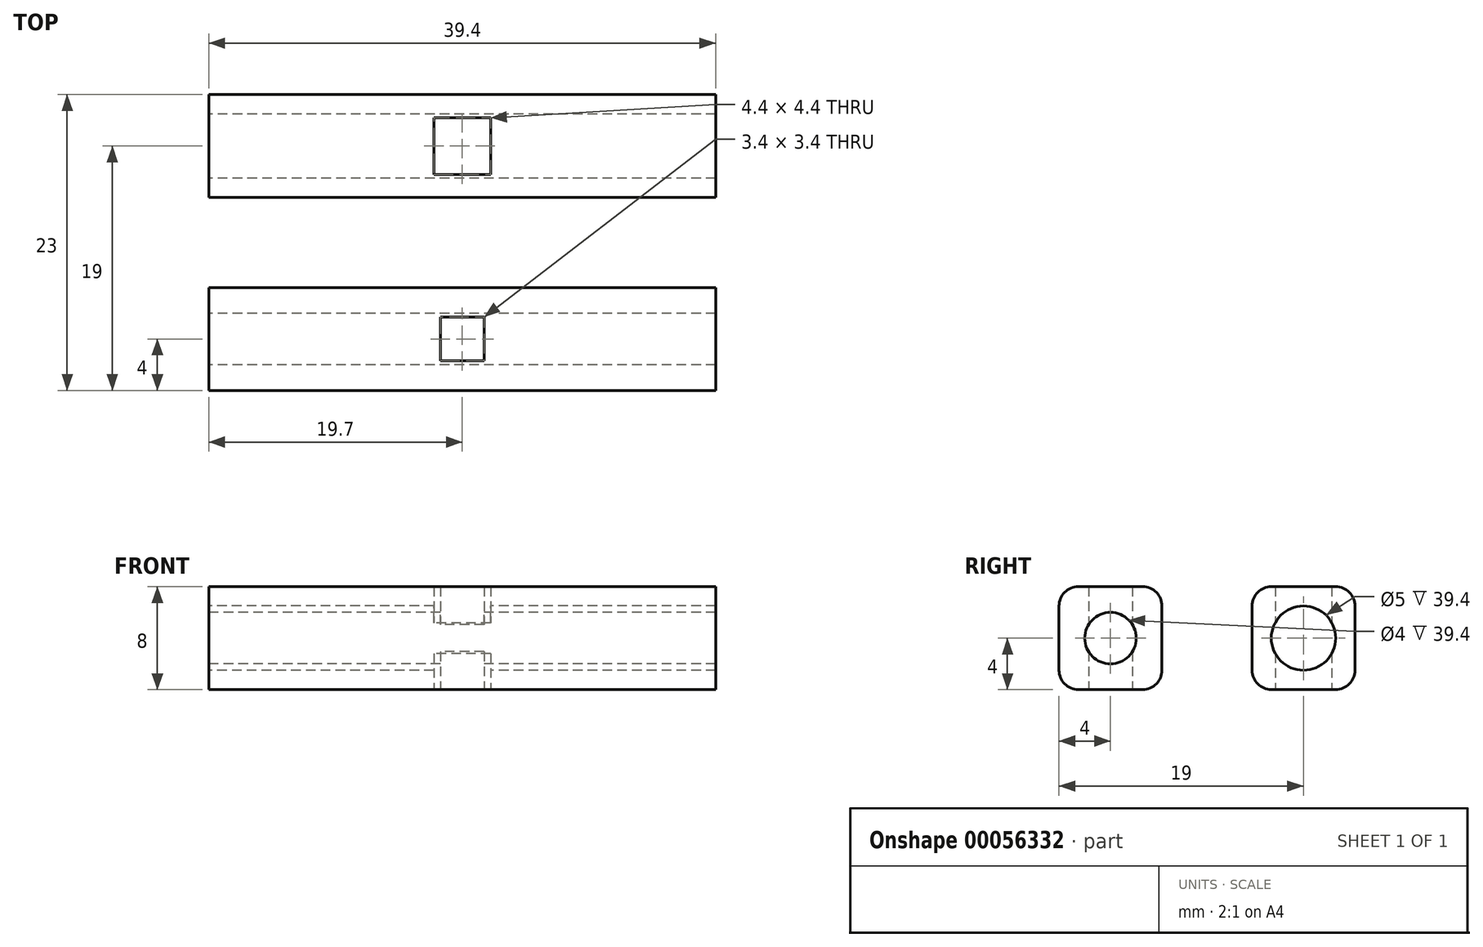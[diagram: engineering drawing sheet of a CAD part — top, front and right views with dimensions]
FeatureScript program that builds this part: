
annotation { "Feature Type Name" : "Feature", "Feature Type Description" : "" }
export const myFeature = defineFeature(function(context is Context, id is Id, definition is map)
    precondition{}
    {
        {
            var Q0;
            Q0=qCreatedBy(makeId("Top.planeOp"),FACE);
            var sketch = newSketch(context, id + "F0", { "sketchPlane" : qUnion([Q0])});
            skLineSegment(sketch, "E0.rect.bottom", {"start": v(19.7, 2) * mm, "end": v(-19.7, 2) * mm, "construction": true});
            skLineSegment(sketch, "E0.rect.top", {"start": v(19.7, -2) * mm, "end": v(-19.7, -2) * mm, "construction": true});
            skLineSegment(sketch, "E0.rect.left", {"start": v(19.7, 2) * mm, "end": v(19.7, -2) * mm});
            skLineSegment(sketch, "E0.rect.right", {"start": v(-19.7, 2) * mm, "end": v(-19.7, -2) * mm});
            skPoint(sketch, "E0.rect.middle", {"position": v(0, 0) * mm});
            skLineSegment(sketch, "E1.rect.bottom", {"start": v(19.7, 4) * mm, "end": v(-19.7, 4) * mm});
            skLineSegment(sketch, "E1.rect.top", {"start": v(19.7, -4) * mm, "end": v(-19.7, -4) * mm});
            skLineSegment(sketch, "E1.rect.left", {"start": v(19.7, 4) * mm, "end": v(19.7, -4) * mm});
            skLineSegment(sketch, "E1.rect.right", {"start": v(-19.7, 4) * mm, "end": v(-19.7, -4) * mm});
            skLineSegment(sketch, "E2.rect.bottom", {"start": v(1.7, 1.7) * mm, "end": v(-1.7, 1.7) * mm});
            skLineSegment(sketch, "E2.rect.top", {"start": v(1.7, -1.7) * mm, "end": v(-1.7, -1.7) * mm});
            skLineSegment(sketch, "E2.rect.left", {"start": v(1.7, 1.7) * mm, "end": v(1.7, -1.7) * mm});
            skLineSegment(sketch, "E2.rect.right", {"start": v(-1.7, 1.7) * mm, "end": v(-1.7, -1.7) * mm});
            skSolve(sketch);
        }
        {
            var Q0;
            Q0=qSketchRegion(id+"F0",true);
            extrude(context, id + "F1", {"entities" : qUnion([Q0]), "depth" : 8 * mm});
        }
        {
            var Q0;
            Q0=makeQuery(id+"F1.opExtrude","SWEPT_FACE",FACE,{"disambiguationData":[OSD([sQuery(id+"F0.wireOp",EDGE,"E1.rect.right")])]});
            var sketch = newSketch(context, id + "F2", { "sketchPlane" : qUnion([Q0])});
            skCircle(sketch, "E3", {"center": v(0, 4) * mm, "radius": 2 * mm});
            skPoint(sketch, "E3.centerSnap0", {"position": v(4, 4) * mm});
            skPoint(sketch, "E3.centerSnap1", {"position": v(0, 8) * mm});
            skSolve(sketch);
        }
        {
            var Q0;
            Q0=qSketchRegion(id+"F2",true);
            extrude(context, id + "F3", {"entities" : qUnion([Q0]), "operationType" : NewBodyOperationType.REMOVE, "endBound" : BoundingType.THROUGH_ALL, "oppositeDirection" : true, "depth" : 25 * mm});
        }
        {
            var Q0;
            Q0=makeQuery(id+"F1.opExtrude","CAP_EDGE",EDGE,{"disambiguationData":[OSD([sQuery(id+"F0.wireOp",EDGE,"E1.rect.top")])],"isStart":false});
            var Q1;
            Q1=makeQuery(id+"F1.opExtrude","CAP_EDGE",EDGE,{"disambiguationData":[OSD([sQuery(id+"F0.wireOp",EDGE,"E1.rect.bottom")])],"isStart":false});
            var Q2;
            Q2=makeQuery(id+"F1.opExtrude","CAP_EDGE",EDGE,{"disambiguationData":[OSD([sQuery(id+"F0.wireOp",EDGE,"E1.rect.top")])],"isStart":true});
            var Q3;
            Q3=makeQuery(id+"F1.opExtrude","CAP_EDGE",EDGE,{"disambiguationData":[OSD([sQuery(id+"F0.wireOp",EDGE,"E1.rect.bottom")])],"isStart":true});
            fillet(context, id + "F4", {"entities" : qUnion([Q0, Q1, Q2, Q3]), "radius" : 1.5 * mm, "tangentPropagation" : true, "allowEdgeOverflow" : false});
        }
        {
            var Q0;
            Q0=makeQuery(id+"F1.opExtrude","SWEPT_BODY",BODY,{"disambiguationData":[OSD([sQuery(id+"F0.wireOp",EDGE,"E1.rect.bottom"),sQuery(id+"F0.wireOp",EDGE,"E1.rect.top"),sQuery(id+"F0.wireOp",EDGE,"E1.rect.left"),sQuery(id+"F0.wireOp",EDGE,"E1.rect.right"),sQuery(id+"F0.wireOp",EDGE,"E2.rect.bottom"),sQuery(id+"F0.wireOp",EDGE,"E2.rect.top"),sQuery(id+"F0.wireOp",EDGE,"E2.rect.left"),sQuery(id+"F0.wireOp",EDGE,"E2.rect.right")])]});
            transform(context, id + "F5", {"entities" : qUnion([Q0]), "transformType" : TransformType.TRANSLATION_3D, "dx" : 0 * mm, "dy" : 15 * mm, "dz" : 0 * mm, "makeCopy" : true});
        }
        {
            var Q0;
            Q0=makeQuery(id+"F5.opPattern","COPY",FACE,{"derivedFrom":makeQuery(id+"F1.opExtrude","SWEPT_FACE",FACE,{"disambiguationData":[OSD([sQuery(id+"F0.wireOp",EDGE,"E1.rect.right")])]}),"instanceName":"1"});
            var sketch = newSketch(context, id + "F6", { "sketchPlane" : qUnion([Q0])});
            skCircle(sketch, "E4", {"center": v(-15, 4) * mm, "radius": 2.5 * mm});
            skSolve(sketch);
        }
        {
            var Q0;
            Q0=makeQuery(id+"F6.imprint","IMPRINT",FACE,{"disambiguationData":[TD([[makeQuery(id+"F6.imprint","IMPRINT",EDGE,{"derivedFrom":sQuery(id+"F6.wireOp",EDGE,"E4")}),1.0]])]});
            extrude(context, id + "F7", {"entities" : qUnion([Q0]), "operationType" : NewBodyOperationType.REMOVE, "endBound" : BoundingType.THROUGH_ALL, "oppositeDirection" : true, "depth" : 25 * mm});
        }
        {
            var Q0;
            Q0=makeQuery(id+"F5.opPattern","COPY",FACE,{"derivedFrom":makeQuery(id+"F1.opExtrude","CAP_FACE",FACE,{"disambiguationData":[OSD([sQuery(id+"F0.wireOp",EDGE,"E1.rect.bottom"),sQuery(id+"F0.wireOp",EDGE,"E1.rect.top"),sQuery(id+"F0.wireOp",EDGE,"E1.rect.left"),sQuery(id+"F0.wireOp",EDGE,"E1.rect.right"),sQuery(id+"F0.wireOp",EDGE,"E2.rect.bottom"),sQuery(id+"F0.wireOp",EDGE,"E2.rect.top"),sQuery(id+"F0.wireOp",EDGE,"E2.rect.left"),sQuery(id+"F0.wireOp",EDGE,"E2.rect.right")])],"isStart":true}),"instanceName":"1"});
            var sketch = newSketch(context, id + "F8", { "sketchPlane" : qUnion([Q0])});
            skLineSegment(sketch, "E5.rect.bottom", {"start": v(2.2, -12.8) * mm, "end": v(-2.2, -12.8) * mm});
            skLineSegment(sketch, "E5.rect.top", {"start": v(2.2, -17.2) * mm, "end": v(-2.2, -17.2) * mm});
            skLineSegment(sketch, "E5.rect.left", {"start": v(2.2, -12.8) * mm, "end": v(2.2, -17.2) * mm});
            skLineSegment(sketch, "E5.rect.right", {"start": v(-2.2, -12.8) * mm, "end": v(-2.2, -17.2) * mm});
            skPoint(sketch, "E5.rect.middle", {"position": v(0, -15) * mm});
            skPoint(sketch, "E5.rect.middle.positionSnap0", {"position": v(0, -13.3) * mm});
            skPoint(sketch, "E5.rect.middle.positionSnap1", {"position": v(1.7, -15) * mm});
            skPoint(sketch, "E5.rect.centerSnap0", {"position": v(0, -13.3) * mm});
            skPoint(sketch, "E5.rect.centerSnap1", {"position": v(1.7, -15) * mm});
            skSolve(sketch);
        }
        {
            var Q0;
            Q0=makeQuery(id+"F8.imprint","IMPRINT",FACE,{"disambiguationData":[TD([[makeQuery(id+"F8.imprint","IMPRINT",EDGE,{"derivedFrom":sQuery(id+"F8.wireOp",EDGE,"E5.rect.bottom")}),1.0]])]});
            extrude(context, id + "F9", {"entities" : qUnion([Q0]), "operationType" : NewBodyOperationType.REMOVE, "endBound" : BoundingType.THROUGH_ALL, "oppositeDirection" : true, "depth" : 25 * mm});
        }
    });
